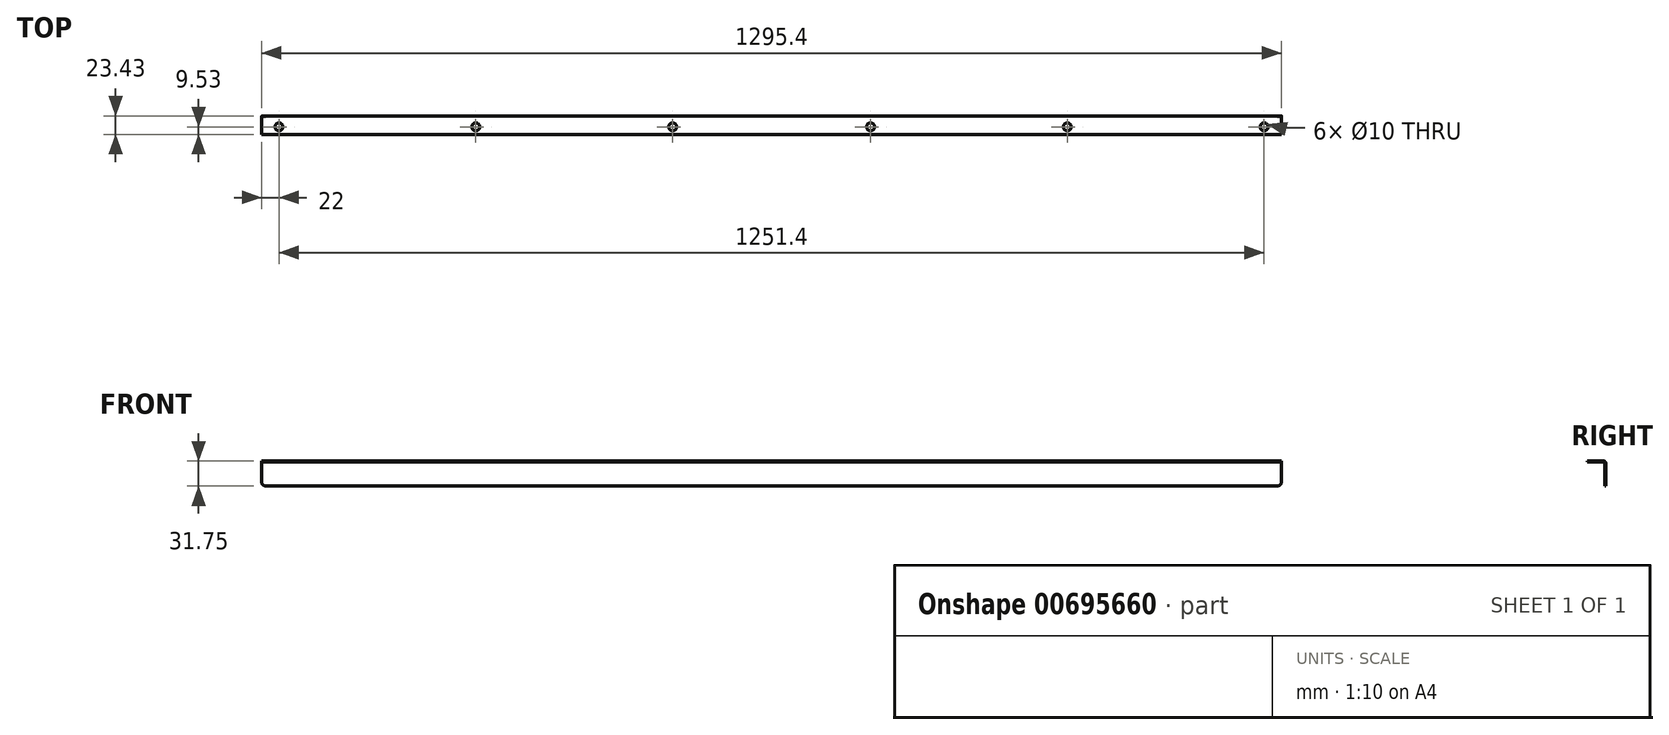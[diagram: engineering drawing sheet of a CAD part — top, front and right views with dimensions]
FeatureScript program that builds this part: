
annotation { "Feature Type Name" : "Feature", "Feature Type Description" : "" }
export const myFeature = defineFeature(function(context is Context, id is Id, definition is map)
    precondition{}
    {
        {
            var Q0;
            Q0=qCreatedBy(makeId("Right.planeOp"),FACE);
            var sketch = newSketch(context, id + "F0", { "sketchPlane" : qUnion([Q0])});
            skLineSegment(sketch, "E0", {"start": v(0, 0) * mm, "end": v(0, 28.52) * mm});
            skLineSegment(sketch, "E1", {"start": v(-2.03, 30.55) * mm, "end": v(-22.23, 30.55) * mm});
            skLineSegment(sketch, "E2", {"start": v(-22.23, 30.55) * mm, "end": v(-22.23, 31.75) * mm});
            skLineSegment(sketch, "E3", {"start": v(-22.23, 31.75) * mm, "end": v(-1.34, 31.75) * mm});
            skLineSegment(sketch, "E4", {"start": v(1.2, 29.21) * mm, "end": v(1.2, 0) * mm});
            skLineSegment(sketch, "E5", {"start": v(1.2, 0) * mm, "end": v(0, 0) * mm});
            skPoint(sketch, "E6.visualSharp", {"position": v(1.2, 31.75) * mm});
            skArc(sketch, "E6.filletArc", {"start": v(1.2, 29.21) * mm, "mid": v(0.46, 31) * mm, "end": v(-1.34, 31.75) * mm});
            skPoint(sketch, "E7.visualSharp", {"position": v(0, 30.55) * mm});
            skArc(sketch, "E7.filletArc", {"start": v(0, 28.52) * mm, "mid": v(-0.6, 29.95) * mm, "end": v(-2.03, 30.55) * mm});
            skSolve(sketch);
        }
        {
            var Q0;
            Q0 = qSketchRegion(id + "F0", true);
            extrude(context, id + "F1", {"entities" : qUnion([Q0]), "depth" : 1295.4 * mm, "offsetDistance" : 25.4 * mm});
        }
        {
            var Q0;
            Q0=makeQuery(id+"F1.opExtrude","SWEPT_FACE",FACE,{"disambiguationData":[OSD([sQuery(id+"F0.wireOp",EDGE,"E3")])]});
            var sketch = newSketch(context, id + "F2", { "sketchPlane" : qUnion([Q0])});
            skCircle(sketch, "E8", {"center": v(22, -12.7) * mm, "radius": 5 * mm});
            skCircle(sketch, "E9", {"center": v(272, -12.7) * mm, "radius": 5 * mm});
            skCircle(sketch, "E10", {"center": v(522, -12.7) * mm, "radius": 5 * mm});
            skCircle(sketch, "E11", {"center": v(1273.4, -12.7) * mm, "radius": 5 * mm});
            skCircle(sketch, "E12", {"center": v(1023.4, -12.7) * mm, "radius": 5 * mm});
            skCircle(sketch, "E13", {"center": v(773.4, -12.7) * mm, "radius": 5 * mm});
            skSolve(sketch);
        }
        {
            var Q0;
            Q0 = qSketchRegion(id + "F2", true);
            extrude(context, id + "F3", {"entities" : qUnion([Q0]), "operationType" : NewBodyOperationType.REMOVE, "oppositeDirection" : true, "depth" : 25.4 * mm, "offsetDistance" : 25.4 * mm});
        }
        {
            var Q0;
            Q0=makeQuery(id+"F1.opExtrude","CAP_EDGE",EDGE,{"disambiguationData":[OSD([sQuery(id+"F0.wireOp",EDGE,"E5")])],"isStart":false});
            var Q1;
            Q1=makeQuery(id+"F1.opExtrude","CAP_EDGE",EDGE,{"disambiguationData":[OSD([sQuery(id+"F0.wireOp",EDGE,"E5")])],"isStart":true});
            fillet(context, id + "F4", {"entities" : qUnion([Q0, Q1]), "radius" : 5.08 * mm, "tangentPropagation" : true, "allowEdgeOverflow" : false});
        }
    });
